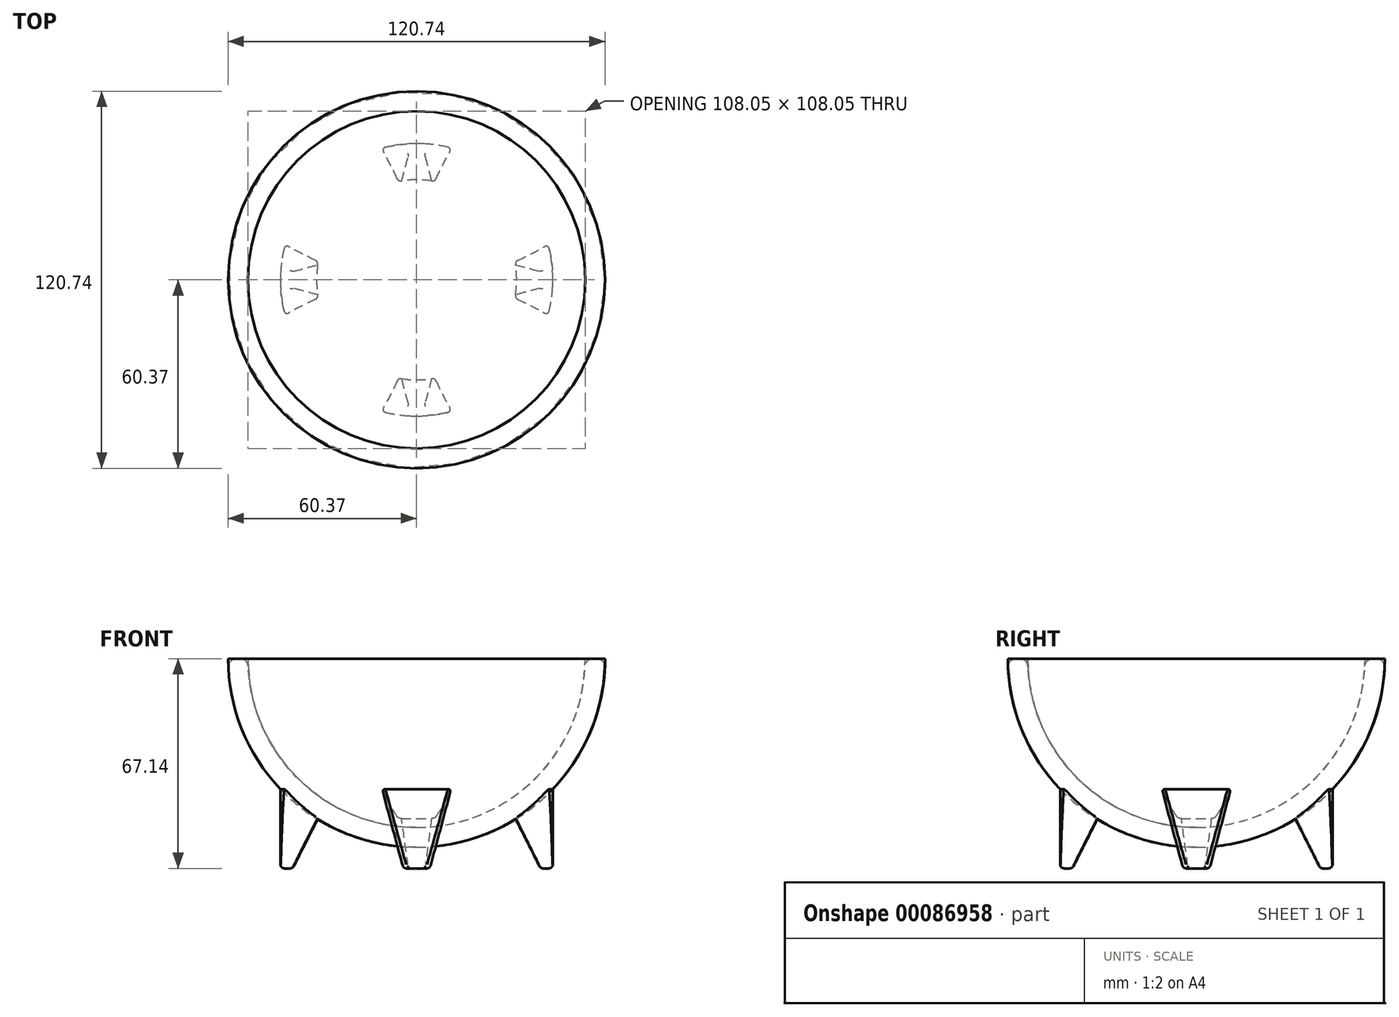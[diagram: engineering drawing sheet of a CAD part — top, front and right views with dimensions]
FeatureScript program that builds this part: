
annotation { "Feature Type Name" : "Feature", "Feature Type Description" : "" }
export const myFeature = defineFeature(function(context is Context, id is Id, definition is map)
    precondition{}
    {
        {
            var Q0;
            Q0=qCreatedBy(makeId("Front.planeOp"),FACE);
            var sketch = newSketch(context, id + "F0", { "sketchPlane" : qUnion([Q0])});
            skArc(sketch, "E0", {"start": v(-60.37, 0) * mm, "mid": v(-42.7, -42.7) * mm, "end": v(0, -60.37) * mm});
            skLineSegment(sketch, "E1", {"start": v(0, 0) * mm, "end": v(-60.37, 0) * mm});
            skLineSegment(sketch, "E2", {"start": v(0, 0) * mm, "end": v(0, -60.37) * mm});
            skSolve(sketch);
        }
        {
            var Q0;
            {var subQ0=sQuery(id+"F0.wireOp",EDGE,"E1");Q0=makeQuery(id+"F0.imprint","IMPRINT",FACE,{"disambiguationData":[TD([[makeQuery(id+"F0.imprint","IMPRINT",EDGE,{"derivedFrom":subQ0}),1.0]])]});}
            var Q1;
            Q1=sQuery(id+"F0.wireOp",EDGE,"E2");
            revolve(context, id + "F1", {"entities" : qUnion([Q0]), "axis" : qUnion([Q1]), "revolveType" : RevolveType.FULL});
        }
        {
            var Q0;
            Q0=makeQuery(id+"F1.opRevolve","SWEPT_FACE",FACE,{"disambiguationData":[OSD([sQuery(id+"F0.wireOp",EDGE,"E1")])]});
            shell(context, id + "F2", {"entities" : qUnion([Q0]), "thickness" : 6.35 * mm});
        }
        {
            var Q0;
            Q0=qCreatedBy(makeId("Front.planeOp"),FACE);
            var sketch = newSketch(context, id + "F3", { "sketchPlane" : qUnion([Q0])});
            skLineSegment(sketch, "E3", {"start": v(-43.62, -41.74) * mm, "end": v(-43.62, -67.14) * mm});
            skLineSegment(sketch, "E4", {"start": v(-43.62, -67.14) * mm, "end": v(-39.81, -67.14) * mm});
            skLineSegment(sketch, "E5", {"start": v(-39.81, -67.14) * mm, "end": v(-32.03, -51.17) * mm});
            skLineSegment(sketch, "E6", {"start": v(-32.03, -51.17) * mm, "end": v(-43.62, -41.74) * mm});
            skSolve(sketch);
        }
        {
            var Q0;
            Q0=makeQuery(id+"F3.imprint","IMPRINT",FACE,{"disambiguationData":[TD([[makeQuery(id+"F3.imprint","IMPRINT",EDGE,{"derivedFrom":sQuery(id+"F3.wireOp",EDGE,"E3")}),1.0]])]});
            var Q1;
            Q1=sQuery(id+"F0.wireOp",EDGE,"E2");
            revolve(context, id + "F4", {"operationType" : NewBodyOperationType.ADD, "entities" : qUnion([Q0]), "axis" : qUnion([Q1]), "revolveType" : RevolveType.SYMMETRIC, "angle" : 30 * degree});
        }
        {
            var Q0;
            Q0=makeQuery(id+"F4.opRevolve","CAP_EDGE",EDGE,{"disambiguationData":[OSD([sQuery(id+"F3.wireOp",EDGE,"E4")])],"isStart":false});
            var Q1;
            Q1=makeQuery(id+"F4.opRevolve","CAP_EDGE",EDGE,{"disambiguationData":[OSD([sQuery(id+"F3.wireOp",EDGE,"E4")])],"isStart":true});
            chamfer(context, id + "F5", {"entities" : qUnion([Q0, Q1]), "chamferType" : ChamferType.OFFSET_ANGLE, "width" : 25.4 * mm, "oppositeDirection" : true, "angle" : 15 * degree, "tangentPropagation" : true});
        }
        {
            var Q0;
            Q0=makeQuery(id+"F4.opRevolve","SWEPT_EDGE",EDGE,{"disambiguationData":[OSD([sQuery(id+"F3.wireOp",EDGE,"E3"),sQuery(id+"F3.wireOp",EDGE,"E4")])]});
            var Q1;
            {var subQ0=sQuery(id+"F3.wireOp",EDGE,"E4");Q1=makeQuery(id+"F5.opChamfer","BLEND_EDGE",EDGE,{"blendedFrom":[makeQuery(id+"F4.opRevolve","CAP_EDGE",EDGE,{"disambiguationData":[OSD([subQ0])],"isStart":false}),makeQuery(id+"F4.opRevolve","SWEPT_FACE",FACE,{"disambiguationData":[OSD([subQ0])]})],"blendedInto":[makeQuery(id+"F4.opRevolve","SWEPT_FACE",FACE,{"disambiguationData":[OSD([subQ0])]})]});}
            var Q2;
            Q2=makeQuery(id+"F4.opRevolve","SWEPT_EDGE",EDGE,{"disambiguationData":[OSD([sQuery(id+"F3.wireOp",EDGE,"E4"),sQuery(id+"F3.wireOp",EDGE,"E5")])]});
            var Q3;
            {var subQ0=sQuery(id+"F3.wireOp",EDGE,"E4");Q3=makeQuery(id+"F5.opChamfer","BLEND_EDGE",EDGE,{"blendedFrom":[makeQuery(id+"F4.opRevolve","CAP_EDGE",EDGE,{"disambiguationData":[OSD([subQ0])],"isStart":true}),makeQuery(id+"F4.opRevolve","SWEPT_FACE",FACE,{"disambiguationData":[OSD([subQ0])]})],"blendedInto":[makeQuery(id+"F4.opRevolve","SWEPT_FACE",FACE,{"disambiguationData":[OSD([subQ0])]})]});}
            var Q4;
            Q4=makeQuery(id+"F5.opChamfer","BLEND_EDGE",EDGE,{"blendedFrom":[makeQuery(id+"F4.opRevolve","CAP_EDGE",EDGE,{"disambiguationData":[OSD([sQuery(id+"F3.wireOp",EDGE,"E4")])],"isStart":false}),makeQuery(id+"F4.opRevolve","SWEPT_FACE",FACE,{"disambiguationData":[OSD([sQuery(id+"F3.wireOp",EDGE,"E5")])]})],"blendedInto":[makeQuery(id+"F4.opRevolve","SWEPT_FACE",FACE,{"disambiguationData":[OSD([sQuery(id+"F3.wireOp",EDGE,"E5")])]})]});
            var Q5;
            Q5=makeQuery(id+"F5.opChamfer","BLEND_EDGE",EDGE,{"blendedFrom":[makeQuery(id+"F4.opRevolve","CAP_EDGE",EDGE,{"disambiguationData":[OSD([sQuery(id+"F3.wireOp",EDGE,"E4")])],"isStart":false}),makeQuery(id+"F4.opRevolve","SWEPT_FACE",FACE,{"disambiguationData":[OSD([sQuery(id+"F3.wireOp",EDGE,"E3")])]})],"blendedInto":[makeQuery(id+"F4.opRevolve","SWEPT_FACE",FACE,{"disambiguationData":[OSD([sQuery(id+"F3.wireOp",EDGE,"E3")])]})]});
            var Q6;
            Q6=makeQuery(id+"F5.opChamfer","BLEND_EDGE",EDGE,{"blendedFrom":[makeQuery(id+"F4.opRevolve","CAP_EDGE",EDGE,{"disambiguationData":[OSD([sQuery(id+"F3.wireOp",EDGE,"E4")])],"isStart":true}),makeQuery(id+"F4.opRevolve","SWEPT_FACE",FACE,{"disambiguationData":[OSD([sQuery(id+"F3.wireOp",EDGE,"E5")])]})],"blendedInto":[makeQuery(id+"F4.opRevolve","SWEPT_FACE",FACE,{"disambiguationData":[OSD([sQuery(id+"F3.wireOp",EDGE,"E5")])]})]});
            var Q7;
            Q7=makeQuery(id+"F5.opChamfer","BLEND_EDGE",EDGE,{"blendedFrom":[makeQuery(id+"F4.opRevolve","CAP_EDGE",EDGE,{"disambiguationData":[OSD([sQuery(id+"F3.wireOp",EDGE,"E4")])],"isStart":true}),makeQuery(id+"F4.opRevolve","SWEPT_FACE",FACE,{"disambiguationData":[OSD([sQuery(id+"F3.wireOp",EDGE,"E3")])]})],"blendedInto":[makeQuery(id+"F4.opRevolve","SWEPT_FACE",FACE,{"disambiguationData":[OSD([sQuery(id+"F3.wireOp",EDGE,"E3")])]})]});
            fillet(context, id + "F6", {"entities" : qUnion([Q0, Q1, Q2, Q3, Q4, Q5, Q6, Q7]), "radius" : 1.27 * mm, "tangentPropagation" : true, "allowEdgeOverflow" : false});
        }
        {
            var Q0;
            Q0=makeQuery(id+"F1.opRevolve","SWEPT_BODY",BODY,{"disambiguationData":[OSD([sQuery(id+"F0.wireOp",EDGE,"E0"),sQuery(id+"F0.wireOp",EDGE,"E1"),sQuery(id+"F0.wireOp",EDGE,"E2")])]});
            var Q1;
            Q1=sQuery(id+"F0.wireOp",EDGE,"E2");
            circularPattern(context, id + "F7", {"entities" : qUnion([Q0]), "axis" : qUnion([Q1]), "angle" : 90 * degree, "instanceCount" : 4});
        }
        {
            var Q0;
            Q0=makeQuery(id+"F2.opShell","OFFSET_EDGE",EDGE,{"disambiguationData":[OSD([sQuery(id+"F0.wireOp",EDGE,"E0"),sQuery(id+"F0.wireOp",EDGE,"E1")])]});
            var Q1;
            Q1=makeQuery(id+"F1.opRevolve","SWEPT_EDGE",EDGE,{"disambiguationData":[OSD([sQuery(id+"F0.wireOp",EDGE,"E0"),sQuery(id+"F0.wireOp",EDGE,"E1")])]});
            fillet(context, id + "F8", {"entities" : qUnion([Q0, Q1]), "radius" : 2.54 * mm, "tangentPropagation" : true, "allowEdgeOverflow" : false});
        }
    });
